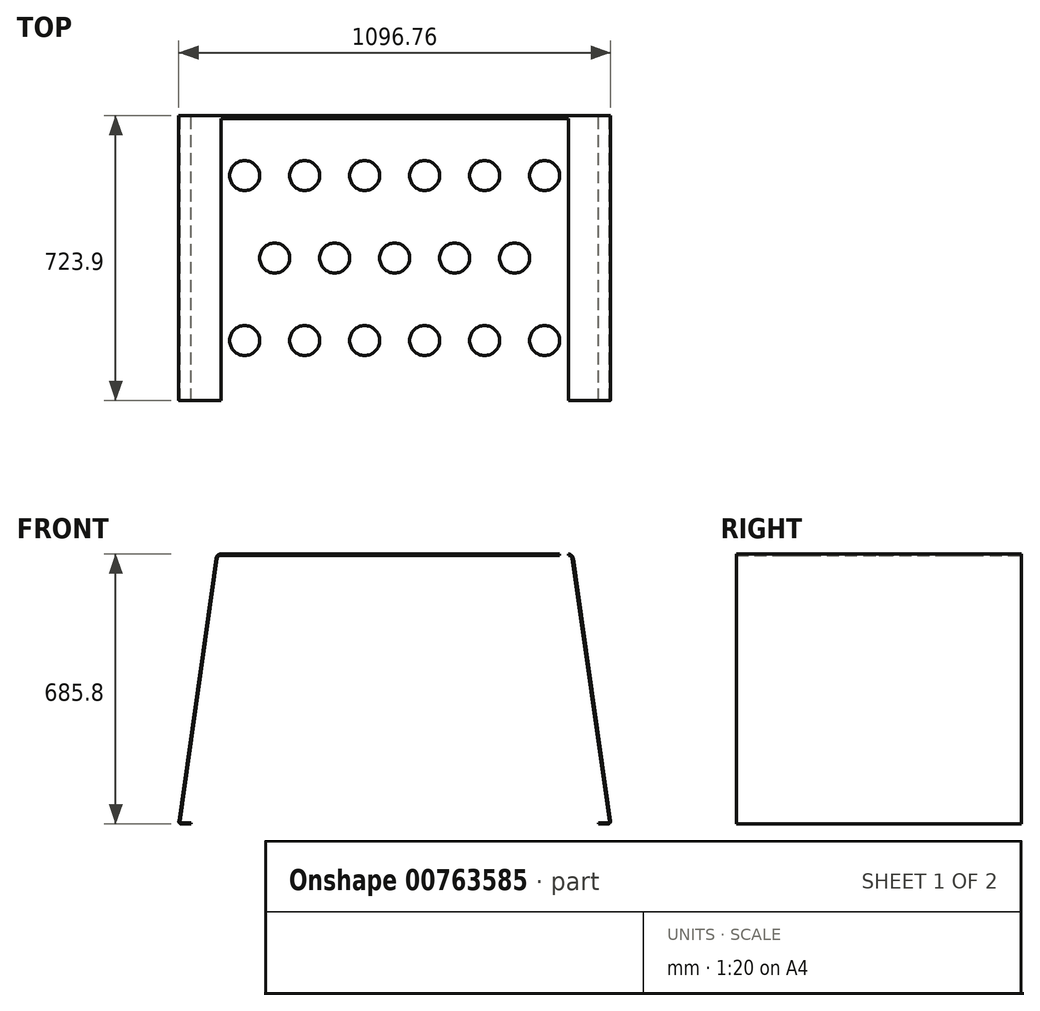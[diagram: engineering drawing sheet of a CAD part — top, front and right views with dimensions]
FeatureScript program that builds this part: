
annotation { "Feature Type Name" : "Feature", "Feature Type Description" : "" }
export const myFeature = defineFeature(function(context is Context, id is Id, definition is map)
    precondition{}
    {
        {
            var Q0;
            Q0=qCreatedBy(makeId("Front.planeOp"),FACE);
            var sketch = newSketch(context, id + "F0", { "sketchPlane" : qUnion([Q0])});
            skLineSegment(sketch, "E0", {"start": v(-8228.57, 764.02) * mm, "end": v(-8323.18, 96.38) * mm});
            skLineSegment(sketch, "E1", {"start": v(-8216, 774.94) * mm, "end": v(-7333.74, 774.94) * mm});
            skLineSegment(sketch, "E2", {"start": v(-7321.17, 764.02) * mm, "end": v(-7226.55, 96.38) * mm});
            skArc(sketch, "E3", {"start": v(-8216, 774.94) * mm, "mid": v(-8224.32, 771.83) * mm, "end": v(-8228.57, 764.02) * mm});
            skArc(sketch, "E4", {"start": v(-7321.17, 764.02) * mm, "mid": v(-7325.41, 771.83) * mm, "end": v(-7333.74, 774.94) * mm});
            skLineSegment(sketch, "E5", {"start": v(-8316.9, 89.14) * mm, "end": v(-8292.14, 89.14) * mm});
            skArc(sketch, "E6", {"start": v(-8323.18, 96.38) * mm, "mid": v(-8321.7, 91.33) * mm, "end": v(-8316.9, 89.14) * mm});
            skLineSegment(sketch, "E7", {"start": v(-7232.84, 89.14) * mm, "end": v(-7257.6, 89.14) * mm});
            skArc(sketch, "E8", {"start": v(-7232.84, 89.14) * mm, "mid": v(-7228.04, 91.33) * mm, "end": v(-7226.55, 96.38) * mm});
            skLineSegment(sketch, "E9", {"start": v(-8317.81, 92.31) * mm, "end": v(-8292.14, 92.31) * mm});
            skLineSegment(sketch, "E10", {"start": v(-8225.43, 763.57) * mm, "end": v(-8320.17, 95.03) * mm});
            skLineSegment(sketch, "E11", {"start": v(-8292.14, 92.31) * mm, "end": v(-8292.14, 89.14) * mm});
            skArc(sketch, "E12", {"start": v(-8320.17, 95.03) * mm, "mid": v(-8319.6, 93.13) * mm, "end": v(-8317.81, 92.31) * mm});
            skArc(sketch, "E13", {"start": v(-8216, 771.76) * mm, "mid": v(-8222.24, 769.43) * mm, "end": v(-8225.43, 763.57) * mm});
            skLineSegment(sketch, "E14", {"start": v(-8216, 771.76) * mm, "end": v(-7333.74, 771.76) * mm});
            skArc(sketch, "E15", {"start": v(-7324.3, 763.57) * mm, "mid": v(-7327.5, 769.43) * mm, "end": v(-7333.74, 771.76) * mm});
            skLineSegment(sketch, "E16", {"start": v(-7324.3, 763.57) * mm, "end": v(-7229.7, 95.93) * mm});
            skLineSegment(sketch, "E17", {"start": v(-7232.84, 92.31) * mm, "end": v(-7257.6, 92.31) * mm});
            skArc(sketch, "E18", {"start": v(-7232.84, 92.31) * mm, "mid": v(-7230.44, 93.4) * mm, "end": v(-7229.7, 95.93) * mm});
            skLineSegment(sketch, "E19", {"start": v(-7257.6, 92.31) * mm, "end": v(-7257.6, 89.14) * mm});
            skSolve(sketch);
        }
        {
            var Q0;
            Q0=makeQuery(id+"F0.imprint","IMPRINT",FACE,{"disambiguationData":[TD([[makeQuery(id+"F0.imprint","IMPRINT",EDGE,{"derivedFrom":sQuery(id+"F0.wireOp",EDGE,"E0")}),1.0]])]});
            extrude(context, id + "F1", {"entities" : qUnion([Q0]), "depth" : 723.9 * mm, "offsetDistance" : 25.4 * mm});
        }
        {
            var Q0;
            Q0=makeQuery(id+"F1.opExtrude","SWEPT_FACE",FACE,{"disambiguationData":[OSD([sQuery(id+"F0.wireOp",EDGE,"E1")])]});
            var sketch = newSketch(context, id + "F2", { "sketchPlane" : qUnion([Q0])});
            skLineSegment(sketch, "E20", {"start": v(-8316.28, -7.16) * mm, "end": v(-7219.65, -7.16) * mm});
            skLineSegment(sketch, "E21", {"start": v(-8316.28, -724.74) * mm, "end": v(-7219.65, -724.74) * mm});
            skLineSegment(sketch, "E22", {"start": v(-8362.2, -7.16) * mm, "end": v(-7173.73, -7.16) * mm});
            skLineSegment(sketch, "E23", {"start": v(-8362.2, -730.78) * mm, "end": v(-7173.73, -730.78) * mm});
            skLineSegment(sketch, "E24", {"start": v(-8362.2, -2.4) * mm, "end": v(-7173.73, -2.4) * mm});
            skLineSegment(sketch, "E25", {"start": v(-8362.2, -729.5) * mm, "end": v(-7173.73, -729.5) * mm});
            skLineSegment(sketch, "E26", {"start": v(-7306.58, -729.5) * mm, "end": v(-7306.58, -724.74) * mm});
            skLineSegment(sketch, "E27", {"start": v(-8229.35, -729.5) * mm, "end": v(-8229.35, -724.74) * mm});
            skLineSegment(sketch, "E28", {"start": v(-8336.2, -729.5) * mm, "end": v(-8336.2, -724.74) * mm});
            skLineSegment(sketch, "E29", {"start": v(-7199.72, -729.5) * mm, "end": v(-7199.72, -724.74) * mm});
            skLineSegment(sketch, "E30", {"start": v(-7233.5, -729.5) * mm, "end": v(-7233.5, -724.74) * mm});
            skLineSegment(sketch, "E31", {"start": v(-8302.44, -729.5) * mm, "end": v(-8302.44, -724.74) * mm});
            skLineSegment(sketch, "E32", {"start": v(-7173.73, -729.5) * mm, "end": v(-7173.73, -724.74) * mm});
            skLineSegment(sketch, "E33", {"start": v(-8362.2, -729.5) * mm, "end": v(-8362.2, -724.74) * mm});
            skLineSegment(sketch, "E34", {"start": v(-7173.73, -7.16) * mm, "end": v(-7173.73, -2.4) * mm});
            skLineSegment(sketch, "E35", {"start": v(-7199.72, -7.16) * mm, "end": v(-7199.72, -2.4) * mm});
            skLineSegment(sketch, "E36", {"start": v(-7233.5, -7.16) * mm, "end": v(-7233.5, -2.4) * mm});
            skLineSegment(sketch, "E37", {"start": v(-7306.58, -7.16) * mm, "end": v(-7306.58, -2.4) * mm});
            skLineSegment(sketch, "E38", {"start": v(-8229.35, -7.16) * mm, "end": v(-8229.35, -2.4) * mm});
            skLineSegment(sketch, "E39", {"start": v(-8302.44, -7.16) * mm, "end": v(-8302.44, -2.4) * mm});
            skLineSegment(sketch, "E40", {"start": v(-8336.2, -7.16) * mm, "end": v(-8336.2, -2.4) * mm});
            skLineSegment(sketch, "E41", {"start": v(-8362.2, -7.16) * mm, "end": v(-8362.2, -2.4) * mm});
            skLineSegment(sketch, "E42", {"start": v(-8217.42, -724.74) * mm, "end": v(-8217.42, -7.16) * mm});
            skLineSegment(sketch, "E43", {"start": v(-7318.51, -724.74) * mm, "end": v(-7318.51, -7.16) * mm});
            skCircle(sketch, "E44", {"center": v(-8155.87, -152.4) * mm, "radius": 38.1 * mm});
            skCircle(sketch, "E45", {"center": v(-8003.47, -152.4) * mm, "radius": 38.1 * mm});
            skCircle(sketch, "E46", {"center": v(-7851.07, -152.4) * mm, "radius": 38.1 * mm});
            skCircle(sketch, "E47", {"center": v(-7698.67, -152.4) * mm, "radius": 38.1 * mm});
            skCircle(sketch, "E48", {"center": v(-7546.27, -152.4) * mm, "radius": 38.1 * mm});
            skCircle(sketch, "E49", {"center": v(-7393.87, -152.4) * mm, "radius": 38.1 * mm});
            skCircle(sketch, "E50", {"center": v(-8079.67, -361.95) * mm, "radius": 38.1 * mm});
            skCircle(sketch, "E51", {"center": v(-7927.27, -361.95) * mm, "radius": 38.1 * mm});
            skCircle(sketch, "E52", {"center": v(-7774.87, -361.95) * mm, "radius": 38.1 * mm});
            skCircle(sketch, "E53", {"center": v(-7622.47, -361.95) * mm, "radius": 38.1 * mm});
            skCircle(sketch, "E54", {"center": v(-7470.07, -361.95) * mm, "radius": 38.1 * mm});
            skCircle(sketch, "E55", {"center": v(-8155.87, -571.5) * mm, "radius": 38.1 * mm});
            skCircle(sketch, "E56", {"center": v(-8003.47, -571.5) * mm, "radius": 38.1 * mm});
            skCircle(sketch, "E57", {"center": v(-7851.07, -571.5) * mm, "radius": 38.1 * mm});
            skCircle(sketch, "E58", {"center": v(-7698.67, -571.5) * mm, "radius": 38.1 * mm});
            skCircle(sketch, "E59", {"center": v(-7546.27, -571.5) * mm, "radius": 38.1 * mm});
            skCircle(sketch, "E60", {"center": v(-7393.87, -571.5) * mm, "radius": 38.1 * mm});
            skLineSegment(sketch, "E61", {"start": v(-8316.28, -724.74) * mm, "end": v(-8316.28, -7.16) * mm});
            skLineSegment(sketch, "E62", {"start": v(-8285.24, -724.74) * mm, "end": v(-8285.24, -7.16) * mm});
            skLineSegment(sketch, "E63", {"start": v(-7219.65, -724.74) * mm, "end": v(-7219.65, -7.16) * mm});
            skLineSegment(sketch, "E64", {"start": v(-7250.69, -724.74) * mm, "end": v(-7250.69, -7.16) * mm});
            skCircle(sketch, "E65", {"center": v(-8296.35, -70.66) * mm, "radius": 3.18 * mm});
            skCircle(sketch, "E66", {"center": v(-8296.35, -661.24) * mm, "radius": 3.18 * mm});
            skCircle(sketch, "E67", {"center": v(-7237.99, -70.66) * mm, "radius": 3.18 * mm});
            skCircle(sketch, "E68", {"center": v(-7237.99, -661.24) * mm, "radius": 3.18 * mm});
            skLineSegment(sketch, "E69", {"start": v(-8155.87, -571.5) * mm, "end": v(-8003.47, -571.5) * mm, "construction": true});
            skLineSegment(sketch, "E70", {"start": v(-8003.47, -571.5) * mm, "end": v(-7851.07, -571.5) * mm, "construction": true});
            skLineSegment(sketch, "E71", {"start": v(-7851.07, -571.5) * mm, "end": v(-7698.67, -571.5) * mm, "construction": true});
            skLineSegment(sketch, "E72", {"start": v(-7698.67, -571.5) * mm, "end": v(-7546.27, -571.5) * mm, "construction": true});
            skLineSegment(sketch, "E73", {"start": v(-7546.27, -571.5) * mm, "end": v(-7393.87, -571.5) * mm, "construction": true});
            skLineSegment(sketch, "E74", {"start": v(-8079.67, -361.95) * mm, "end": v(-7927.27, -361.95) * mm, "construction": true});
            skLineSegment(sketch, "E75", {"start": v(-7927.27, -361.95) * mm, "end": v(-7774.87, -361.95) * mm, "construction": true});
            skLineSegment(sketch, "E76", {"start": v(-7774.87, -361.95) * mm, "end": v(-7622.47, -361.95) * mm, "construction": true});
            skLineSegment(sketch, "E77", {"start": v(-7622.47, -361.95) * mm, "end": v(-7470.07, -361.95) * mm, "construction": true});
            skLineSegment(sketch, "E78", {"start": v(-8155.87, -152.4) * mm, "end": v(-8003.47, -152.4) * mm, "construction": true});
            skLineSegment(sketch, "E79", {"start": v(-8003.47, -152.4) * mm, "end": v(-7851.07, -152.4) * mm, "construction": true});
            skLineSegment(sketch, "E80", {"start": v(-7851.07, -152.4) * mm, "end": v(-7698.67, -152.4) * mm, "construction": true});
            skLineSegment(sketch, "E81", {"start": v(-7698.67, -152.4) * mm, "end": v(-7546.27, -152.4) * mm, "construction": true});
            skLineSegment(sketch, "E82", {"start": v(-7546.27, -152.4) * mm, "end": v(-7393.87, -152.4) * mm, "construction": true});
            skLineSegment(sketch, "E83", {"start": v(-7774.87, -571.5) * mm, "end": v(-7774.87, -361.95) * mm, "construction": true});
            skLineSegment(sketch, "E84", {"start": v(-7774.87, -361.95) * mm, "end": v(-7774.87, -152.4) * mm, "construction": true});
            skLineSegment(sketch, "E85", {"start": v(-7774.87, -723.9) * mm, "end": v(-7774.87, -571.5) * mm, "construction": true});
            skSolve(sketch);
        }
        {
            var Q0;
            Q0=makeQuery(id+"F2.imprint","IMPRINT",FACE,{"disambiguationData":[TD([[makeQuery(id+"F2.imprint","IMPRINT",EDGE,{"derivedFrom":sQuery(id+"F2.wireOp",EDGE,"E44")}),-1.0]])]});
            var Q1;
            Q1=makeQuery(id+"F2.imprint","IMPRINT",FACE,{"disambiguationData":[TD([[makeQuery(id+"F2.imprint","IMPRINT",EDGE,{"derivedFrom":sQuery(id+"F2.wireOp",EDGE,"E45")}),-1.0]])]});
            var Q2;
            Q2=makeQuery(id+"F2.imprint","IMPRINT",FACE,{"disambiguationData":[TD([[makeQuery(id+"F2.imprint","IMPRINT",EDGE,{"derivedFrom":sQuery(id+"F2.wireOp",EDGE,"E46")}),-1.0]])]});
            var Q3;
            Q3=makeQuery(id+"F2.imprint","IMPRINT",FACE,{"disambiguationData":[TD([[makeQuery(id+"F2.imprint","IMPRINT",EDGE,{"derivedFrom":sQuery(id+"F2.wireOp",EDGE,"E47")}),-1.0]])]});
            var Q4;
            Q4=makeQuery(id+"F2.imprint","IMPRINT",FACE,{"disambiguationData":[TD([[makeQuery(id+"F2.imprint","IMPRINT",EDGE,{"derivedFrom":sQuery(id+"F2.wireOp",EDGE,"E48")}),-1.0]])]});
            var Q5;
            Q5=makeQuery(id+"F2.imprint","IMPRINT",FACE,{"disambiguationData":[TD([[makeQuery(id+"F2.imprint","IMPRINT",EDGE,{"derivedFrom":sQuery(id+"F2.wireOp",EDGE,"E49")}),-1.0]])]});
            var Q6;
            Q6=makeQuery(id+"F2.imprint","IMPRINT",FACE,{"disambiguationData":[TD([[makeQuery(id+"F2.imprint","IMPRINT",EDGE,{"derivedFrom":sQuery(id+"F2.wireOp",EDGE,"E50")}),-1.0]])]});
            var Q7;
            Q7=makeQuery(id+"F2.imprint","IMPRINT",FACE,{"disambiguationData":[TD([[makeQuery(id+"F2.imprint","IMPRINT",EDGE,{"derivedFrom":sQuery(id+"F2.wireOp",EDGE,"E51")}),-1.0]])]});
            var Q8;
            Q8=makeQuery(id+"F2.imprint","IMPRINT",FACE,{"disambiguationData":[TD([[makeQuery(id+"F2.imprint","IMPRINT",EDGE,{"derivedFrom":sQuery(id+"F2.wireOp",EDGE,"E52")}),-1.0]])]});
            var Q9;
            Q9=makeQuery(id+"F2.imprint","IMPRINT",FACE,{"disambiguationData":[TD([[makeQuery(id+"F2.imprint","IMPRINT",EDGE,{"derivedFrom":sQuery(id+"F2.wireOp",EDGE,"E53")}),-1.0]])]});
            var Q10;
            Q10=makeQuery(id+"F2.imprint","IMPRINT",FACE,{"disambiguationData":[TD([[makeQuery(id+"F2.imprint","IMPRINT",EDGE,{"derivedFrom":sQuery(id+"F2.wireOp",EDGE,"E54")}),-1.0]])]});
            var Q11;
            Q11=makeQuery(id+"F2.imprint","IMPRINT",FACE,{"disambiguationData":[TD([[makeQuery(id+"F2.imprint","IMPRINT",EDGE,{"derivedFrom":sQuery(id+"F2.wireOp",EDGE,"E55")}),-1.0]])]});
            var Q12;
            Q12=makeQuery(id+"F2.imprint","IMPRINT",FACE,{"disambiguationData":[TD([[makeQuery(id+"F2.imprint","IMPRINT",EDGE,{"derivedFrom":sQuery(id+"F2.wireOp",EDGE,"E56")}),-1.0]])]});
            var Q13;
            Q13=makeQuery(id+"F2.imprint","IMPRINT",FACE,{"disambiguationData":[TD([[makeQuery(id+"F2.imprint","IMPRINT",EDGE,{"derivedFrom":sQuery(id+"F2.wireOp",EDGE,"E57")}),-1.0]])]});
            var Q14;
            Q14=makeQuery(id+"F2.imprint","IMPRINT",FACE,{"disambiguationData":[TD([[makeQuery(id+"F2.imprint","IMPRINT",EDGE,{"derivedFrom":sQuery(id+"F2.wireOp",EDGE,"E58")}),-1.0]])]});
            var Q15;
            Q15=makeQuery(id+"F2.imprint","IMPRINT",FACE,{"disambiguationData":[TD([[makeQuery(id+"F2.imprint","IMPRINT",EDGE,{"derivedFrom":sQuery(id+"F2.wireOp",EDGE,"E59")}),-1.0]])]});
            var Q16;
            Q16=makeQuery(id+"F2.imprint","IMPRINT",FACE,{"disambiguationData":[TD([[makeQuery(id+"F2.imprint","IMPRINT",EDGE,{"derivedFrom":sQuery(id+"F2.wireOp",EDGE,"E60")}),-1.0]])]});
            extrude(context, id + "F3", {"entities" : qUnion([Q0, Q1, Q2, Q3, Q4, Q5, Q6, Q7, Q8, Q9, Q10, Q11, Q12, Q13, Q14, Q15, Q16]), "operationType" : NewBodyOperationType.REMOVE, "oppositeDirection" : true, "depth" : 25.4 * mm, "offsetDistance" : 25.4 * mm});
        }
    });
